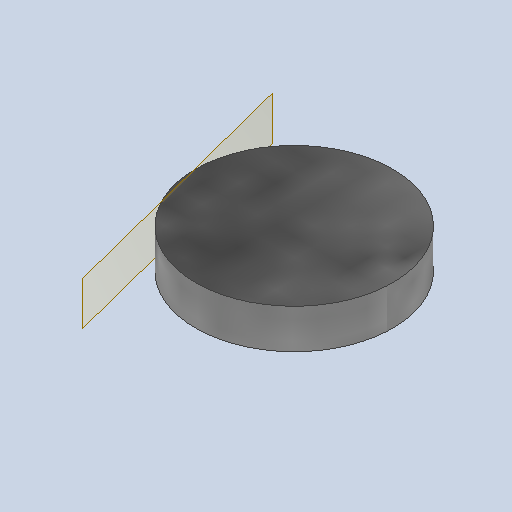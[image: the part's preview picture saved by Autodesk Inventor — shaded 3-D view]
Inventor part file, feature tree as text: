
AUTODESK INVENTOR PART (.ipt)
format: ipt  version: 2025.2 (Build 292293000, 293)  size: 159,744 bytes
history: native  units: mm
features: other x5, extrude x2, sketch x2
ambient origin geometry x8: Origin, YZ Plane, XZ Plane, XY Plane, X Axis, Y Axis, Z Axis, Center Point
bodies: Body1 (feature_tree)
feature tree (9):
  other  "ソリッド1"
  extrude  "押し出し1"  Depth=10.0mm
  other  "作業平面1"
  extrude  "押し出し2"  Depth=2.0mm TaperAngle=0.0deg
  sketch  "スケッチ1"
  sketch  "スケッチ2"
  other  "<userpath>\OneDrive\ドキュメント\New Controller\Hardware\Assembly.iam"
  other  "Assembly.iam"
  other  "Body_compleat01:1"
